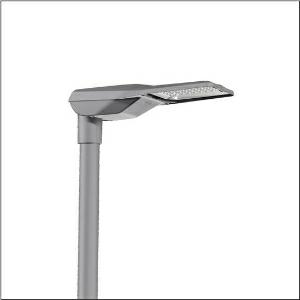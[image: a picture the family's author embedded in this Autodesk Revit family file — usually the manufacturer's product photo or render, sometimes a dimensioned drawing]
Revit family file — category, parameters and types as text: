
# Revit family: streetlight_sl_21_iq_mini___p1_0a_5xe2a41g08hb_15d1
name_source: partatom
category: Lighting Fixtures
units: mm (PartAtom-declared; Revit-internal decimal feet)

## family parameters
Cut with Voids When Loaded = No
Host = Face
Light Source = No
Part Type = Normal
Room Calculation Point = No
Round Connector Dimension = Use Diameter
Shared = No

## types (1)
- --- (1 x LED, 9860 lm, 70.9 W, 4000K)
    Apparent Load = 71 VA
    CIE Flux Codes = 21 50 90 100 100
    Color Rendering = 70
    Color Temperature = 4000K
    Default Elevation = 1800 mm
    Description = Streetlight SL 21 iQ mini, mast luminaire, primary light control with lens, of PMMA, primary optical cover: cover, of toughened safety glass, transparent, light distribution: P1.0a, light emission: direct distribution, primary light characteristic: asymmetric, installation type: post-top, side-entry, LED, High Power LED, rated luminous flux: 9.860lm, luminous efficacy: 139lm/W, light colour: 740, colour temperature: 4000K, control gear: iQ Street-Remote, control: Street-Remote, Auto-Match, Temp-Guard, Lumen-Switch, Night-Set, Smart-Wire, Light-Fading, Desk-Remote (wireless, voltage-free reading and setting of iQ features in the workshop via application-optimized NFC function/RFID function), optimised constant luminous flux control (CLO 2.0), pre-setting: linear dimming characteristic, mains connection: 220..240V, AC, 50/60Hz, start of lifetime: 71W, end of service life: 75W, reduction: 31W, luminaire housing, of diecast aluminium, powder-coated, Siteco® metallic grey (DB 702S), corrosivity category C5 mid according to DIN EN ISO 12944, please order mast flange separately, inclination adjustable: 0°, 5°, 10°, 15°, sealing non-destructively replaceable, multi-level sealing system, length: 628mm, width: 235mm, height: 110mm, mast flange for spigot size: 42mm (side-entry): 5XC10008XM4, 60/48mm (side-entry/post-top): 5XC10108XM2, 76/60mm (side-entry/post-top): 5XC10108XM1, mounting height: 4..8m, protection rating (complete): IP66, insulation class (complete): insulation class II (safety insulation), certification: CE, ENEC, ENEC+, VDE, impact resistance: IK10, permissible operating ambient temperature for outdoor applications: -40..+50°C, standard-compliant lighting for roads and squares, packaging unit: 1 piece

Light Distribution: P1.0a
    Height = 110 mm
    Lamp = 1 x LED
    Lamp Light Flux = 9860 lm
    Lamp Power = 70.9 W
    Lamp count = 1
    Length = 625 mm
    Luminous efficacy = 139 lm/W
    Manufacturer = Siteco
    ModVariant = No
    Model = 5XE2A41G08HB
    Number of Poles = 1
    OnlyDefault = Yes
    Power Factor = 1
    Product Name = Streetlight SL 21 iQ mini | P1.0a
    Product group = mast luminaire | pylon top
    ProductGroupID = 6100
    Protection Class = Protection class II
    Protection Degree = IP 66
    RLX_Detail_Level = 1
    RLX_Emergency_Light_Flux = 0 lm
    RLX_Emergency_Type = 0
    RLX_Emergency_Type_DB = No
    RlxData = <blob elided: 37553 chars, md5=45cb5a66>
    Socket = socket
    Standby Power = 0 W
    System Light Flux = 9860 lm
    System Power = 71 W
    Type Comments = factory setting: luminous flux: 100 % | dim-lin: 254 | 711 mA
    Type Image = l_1003519.jpg
    URL = http://relux.com
    VarID = @adj_179059
    Voltage = 0 V
    Weight = 0.00 kg
    Width = 234 mm

## geometry (parser evidence)
native form markers: Blend x4, Sweep x10
no freeform markers — native parametric forms only
